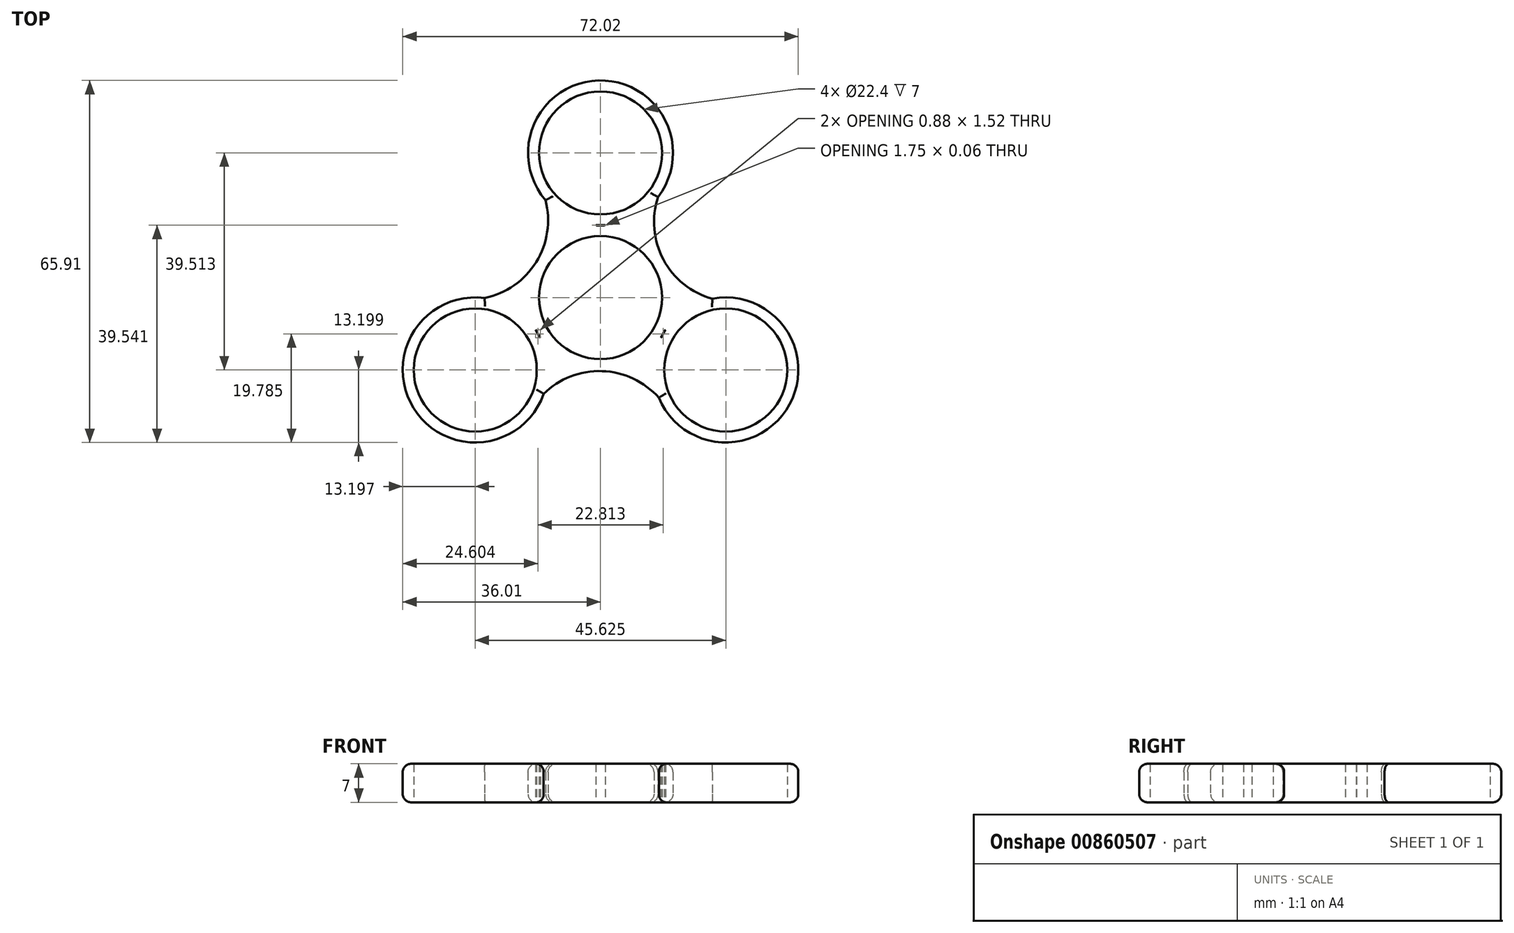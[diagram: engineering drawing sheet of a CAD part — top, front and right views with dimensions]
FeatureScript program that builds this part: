
annotation { "Feature Type Name" : "Feature", "Feature Type Description" : "" }
export const myFeature = defineFeature(function(context is Context, id is Id, definition is map)
    precondition{}
    {
        {
            var Q0;
            Q0=qCreatedBy(makeId("Top.planeOp"),FACE);
            var sketch = newSketch(context, id + "F0", { "sketchPlane" : qUnion([Q0])});
            skCircle(sketch, "E0", {"center": v(0, 0) * mm, "radius": 11.2 * mm});
            skArc(sketch, "E1", {"start": v(-11.84, -5.83) * mm, "mid": v(-11.43, -6.6) * mm, "end": v(-10.97, -7.34) * mm});
            skCircle(sketch, "E2", {"center": v(0, 26.34) * mm, "radius": 11.2 * mm});
            skArc(sketch, "E3", {"start": v(-0.88, 13.17) * mm, "mid": v(0, 13.14) * mm, "end": v(0.88, 13.17) * mm});
            skArc(sketch, "E4.1.0", {"start": v(-21.1, -0.08) * mm, "mid": v(-34.05, -20.09) * mm, "end": v(-10.35, -17.53) * mm});
            skArc(sketch, "E4.2.0", {"start": v(11.84, -5.83) * mm, "mid": v(11.38, -6.57) * mm, "end": v(10.97, -7.34) * mm});
            skCircle(sketch, "E5.1.0", {"center": v(-22.81, -13.17) * mm, "radius": 11.2 * mm});
            skCircle(sketch, "E5.2.0", {"center": v(22.81, -13.17) * mm, "radius": 11.2 * mm});
            skLineSegment(sketch, "E6", {"start": v(-13.13, -7.55) * mm, "end": v(-11.4, -6.54) * mm, "construction": true});
            skArc(sketch, "E7", {"start": v(10.47, 18.3) * mm, "mid": v(11.45, 6.93) * mm, "end": v(20.36, -0.2) * mm});
            skArc(sketch, "E8.1.0", {"start": v(-21.1, -0.08) * mm, "mid": v(-11.73, 6.45) * mm, "end": v(-10, 17.73) * mm});
            skArc(sketch, "E8.2.0", {"start": v(10.62, -18.22) * mm, "mid": v(0.28, -13.38) * mm, "end": v(-10.35, -17.53) * mm});
            skArc(sketch, "E9.trimOffspring", {"start": v(10.47, 18.3) * mm, "mid": v(-0.37, 39.54) * mm, "end": v(-10, 17.73) * mm});
            skLineSegment(sketch, "E10.trimOffspring", {"start": v(10.97, 7.34) * mm, "end": v(11.84, 5.83) * mm, "construction": true});
            skLineSegment(sketch, "E11.trimOffspring", {"start": v(9.65, 5.68) * mm, "end": v(11.53, 6.77) * mm, "construction": true});
            skLineSegment(sketch, "E12.trimOffspring", {"start": v(16.21, -1.74) * mm, "end": v(17.21, -3.47) * mm, "construction": true});
            skArc(sketch, "E13.trimOffspring", {"start": v(-10.97, -7.34) * mm, "mid": v(-11.38, -6.57) * mm, "end": v(-11.84, -5.83) * mm});
            skArc(sketch, "E14.trimOffspring", {"start": v(10.62, -18.22) * mm, "mid": v(34.43, -19.45) * mm, "end": v(20.36, -0.2) * mm});
            skArc(sketch, "E15.trimOffspring", {"start": v(10.97, -7.34) * mm, "mid": v(11.43, -6.6) * mm, "end": v(11.84, -5.83) * mm});
            skArc(sketch, "E16.trimOffspring", {"start": v(11.84, 5.83) * mm, "mid": v(11.43, 6.6) * mm, "end": v(10.97, 7.34) * mm});
            skArc(sketch, "E17.trimOffspring", {"start": v(0.88, 13.17) * mm, "mid": v(0, 13.2) * mm, "end": v(-0.88, 13.17) * mm});
            skSolve(sketch);
        }
        {
            var Q0;
            Q0=makeQuery(id+"F0.imprint","IMPRINT",FACE,{"disambiguationData":[TD([[makeQuery(id+"F0.imprint","IMPRINT",EDGE,{"derivedFrom":sQuery(id+"F0.wireOp",EDGE,"E0")}),-1.0]])]});
            extrude(context, id + "F1", {"entities" : qUnion([Q0]), "depth" : 7 * mm, "offsetDistance" : 25 * mm});
        }
        {
            var Q0;
            Q0=makeQuery(id+"F1.opExtrude","CAP_EDGE",EDGE,{"disambiguationData":[OSD([sQuery(id+"F0.wireOp",EDGE,"E9.trimOffspring")])],"isStart":false});
            var Q1;
            Q1=makeQuery(id+"F1.opExtrude","CAP_EDGE",EDGE,{"disambiguationData":[OSD([sQuery(id+"F0.wireOp",EDGE,"E8.1.0")])],"isStart":false});
            var Q2;
            Q2=makeQuery(id+"F1.opExtrude","CAP_EDGE",EDGE,{"disambiguationData":[OSD([sQuery(id+"F0.wireOp",EDGE,"E4.1.0")])],"isStart":false});
            var Q3;
            Q3=makeQuery(id+"F1.opExtrude","CAP_EDGE",EDGE,{"disambiguationData":[OSD([sQuery(id+"F0.wireOp",EDGE,"E8.2.0")])],"isStart":false});
            var Q4;
            Q4=makeQuery(id+"F1.opExtrude","CAP_EDGE",EDGE,{"disambiguationData":[OSD([sQuery(id+"F0.wireOp",EDGE,"E14.trimOffspring")])],"isStart":false});
            var Q5;
            Q5=makeQuery(id+"F1.opExtrude","CAP_EDGE",EDGE,{"disambiguationData":[OSD([sQuery(id+"F0.wireOp",EDGE,"E7")])],"isStart":false});
            fillet(context, id + "F2", {"entities" : qUnion([Q0, Q1, Q2, Q3, Q4, Q5]), "radius" : 1.5 * mm, "tangentPropagation" : true, "allowEdgeOverflow" : false});
        }
        {
            var Q0;
            Q0=makeQuery(id+"F1.opExtrude","CAP_EDGE",EDGE,{"disambiguationData":[OSD([sQuery(id+"F0.wireOp",EDGE,"E4.1.0")])],"isStart":true});
            var Q1;
            Q1=makeQuery(id+"F1.opExtrude","CAP_EDGE",EDGE,{"disambiguationData":[OSD([sQuery(id+"F0.wireOp",EDGE,"E8.1.0")])],"isStart":true});
            var Q2;
            Q2=makeQuery(id+"F1.opExtrude","CAP_EDGE",EDGE,{"disambiguationData":[OSD([sQuery(id+"F0.wireOp",EDGE,"E9.trimOffspring")])],"isStart":true});
            var Q3;
            Q3=makeQuery(id+"F1.opExtrude","CAP_EDGE",EDGE,{"disambiguationData":[OSD([sQuery(id+"F0.wireOp",EDGE,"E7")])],"isStart":true});
            var Q4;
            Q4=makeQuery(id+"F1.opExtrude","CAP_EDGE",EDGE,{"disambiguationData":[OSD([sQuery(id+"F0.wireOp",EDGE,"E14.trimOffspring")])],"isStart":true});
            var Q5;
            Q5=makeQuery(id+"F1.opExtrude","CAP_EDGE",EDGE,{"disambiguationData":[OSD([sQuery(id+"F0.wireOp",EDGE,"E8.2.0")])],"isStart":true});
            fillet(context, id + "F3", {"entities" : qUnion([Q0, Q1, Q2, Q3, Q4, Q5]), "radius" : 1.5 * mm, "tangentPropagation" : true, "allowEdgeOverflow" : false});
        }
    });
